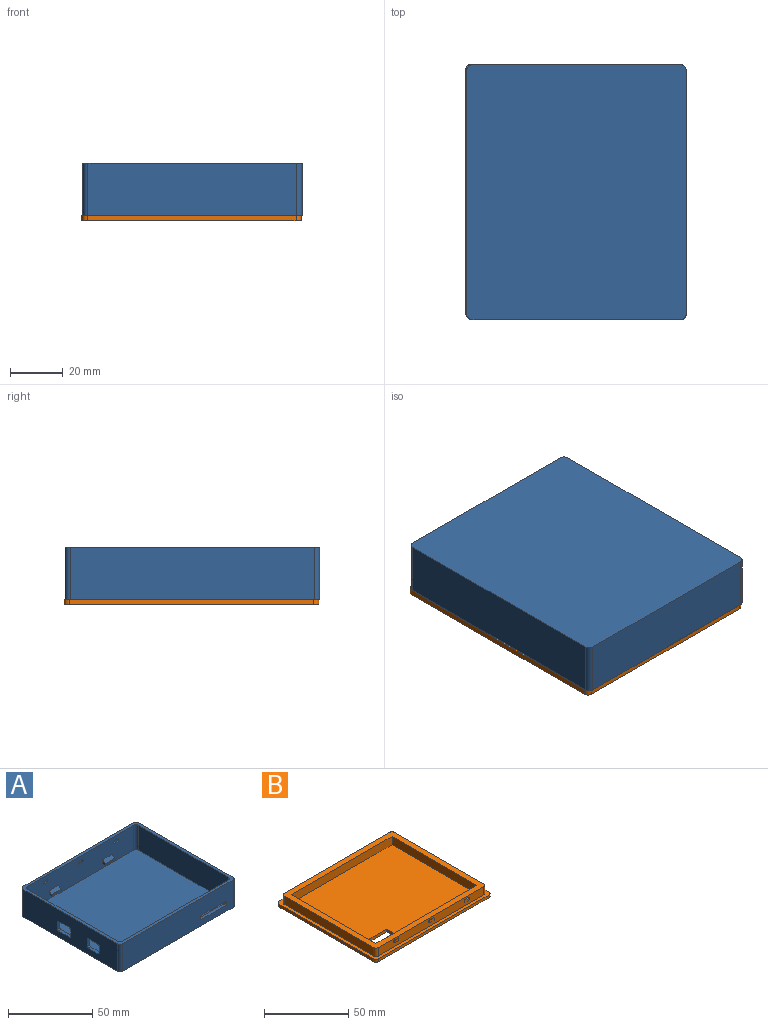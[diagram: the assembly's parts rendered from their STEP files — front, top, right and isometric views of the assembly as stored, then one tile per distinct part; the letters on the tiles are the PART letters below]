
ASSEMBLY  parts=2 mates=1
PART A: 89 faces, bbox 97x83.5x20 mm
  f0: plane 89x18mm, normal (0,1,0), area 1392.9mm2, adj f9,f10,f13,f14,f27,f28,f29,f30
  f1: plane 89x18mm, normal (0,-1,0), area 1530mm2, adj f9,f10,f11,f12,f43,f44,f45,f46
  f2: plane 93x20mm, normal (0,-1,0), area 1794.9mm2, adj f5,f9,f16,f17,f27,f28,f29,f30
  f3: plane 75.5x18mm, normal (1,0,0), area 1213.7mm2, adj f9,f10,f11,f14,f19,f20,f21,f22
  f4: plane 79.5x20mm, normal (-1,0,0), area 1444.7mm2, adj f5,f9,f15,f16,f19,f20,f21,f22
  f5: plane 97x83.5mm, normal (0,0,-1), area 8096.1mm2, adj f2,f4,f7,f8,f15,f16,f17,f18
  f6: plane 75.5x18mm, normal (-1,0,0), area 1359mm2, adj f9,f10,f12,f13
  f7: plane 93x20mm, normal (0,1,0), area 1860mm2, adj f5,f9,f15,f18
  f8: plane 79.5x20mm, normal (1,0,0), area 1590mm2, adj f5,f9,f17,f18
  f9: plane 97x83.5mm, normal (0,0,1), area 706mm2, adj f0,f1,f2,f3,f4,f6,f7,f8
  f10: plane 93x79.5mm, normal (0,0,1), area 7390.1mm2, adj f0,f1,f3,f6,f11,f12,f13,f14
  f11: cylinder r=2mm len=18mm, axis (0,0,-1), area 56.5mm2, adj f1,f3,f9,f10
  f12: cylinder r=2mm len=18mm, axis (0,0,1), area 56.5mm2, adj f1,f6,f9,f10
  f13: cylinder r=2mm len=18mm, axis (0,0,-1), area 56.5mm2, adj f0,f6,f9,f10
  f14: cylinder r=2mm len=18mm, axis (0,0,1), area 56.5mm2, adj f0,f3,f9,f10
  f15: cylinder r=2mm len=20mm, axis (0,0,1), area 62.8mm2, adj f4,f5,f7,f9
  f16: cylinder r=2mm len=20mm, axis (0,0,-1), area 62.8mm2, adj f2,f4,f5,f9
  f17: cylinder r=2mm len=20mm, axis (0,0,1), area 62.8mm2, adj f2,f5,f8,f9
  f18: cylinder r=2mm len=20mm, axis (0,0,-1), area 62.8mm2, adj f5,f7,f8,f9
  f19: plane 5x2mm, normal (0,1,0), area 10mm2, adj f3,f4,f35,f38
  f20: plane 9x2mm, normal (0,0,-1), area 18mm2, adj f3,f4,f35,f36
  f21: plane 5x2mm, normal (0,-1,0), area 10mm2, adj f3,f4,f36,f37
  f22: plane 9x2mm, normal (0,0,1), area 18mm2, adj f3,f4,f37,f38
  f23: plane 5x2mm, normal (0,1,0), area 10mm2, adj f3,f4,f39,f42
  f24: plane 8x2mm, normal (0,0,-1), area 16mm2, adj f3,f4,f41,f42
  f25: plane 5x2mm, normal (0,-1,0), area 10mm2, adj f3,f4,f40,f41
  f26: plane 8x2mm, normal (0,0,1), area 16mm2, adj f3,f4,f39,f40
  f27: plane 2x1mm, normal (-1,0,0), area 2mm2, adj f0,f2,f31,f34
  f28: plane 20x2mm, normal (0,0,-1), area 40mm2, adj f0,f2,f31,f32
  f29: plane 2x1mm, normal (1,0,0), area 2mm2, adj f0,f2,f32,f33
  f30: plane 20x2mm, normal (0,0,1), area 40mm2, adj f0,f2,f33,f34
  f31: cylinder r=1mm len=2mm, axis (0,-1,0), area 3.1mm2, adj f0,f2,f27,f28
  f32: cylinder r=1mm len=2mm, axis (0,1,0), area 3.1mm2, adj f0,f2,f28,f29
  f33: cylinder r=1mm len=2mm, axis (0,-1,0), area 3.1mm2, adj f0,f2,f29,f30
  f34: cylinder r=1mm len=2mm, axis (0,1,0), area 3.1mm2, adj f0,f2,f27,f30
  f35: cylinder r=1mm len=2mm, axis (-1,0,0), area 3.1mm2, adj f3,f4,f19,f20
  f36: cylinder r=1mm len=2mm, axis (1,0,0), area 3.1mm2, adj f3,f4,f20,f21
  f37: cylinder r=1mm len=2mm, axis (-1,0,0), area 3.1mm2, adj f3,f4,f21,f22
  f38: cylinder r=1mm len=2mm, axis (1,0,0), area 3.1mm2, adj f3,f4,f19,f22
  f39: cylinder r=1mm len=2mm, axis (1,0,0), area 3.1mm2, adj f3,f4,f23,f26
  f40: cylinder r=1mm len=2mm, axis (-1,0,0), area 3.1mm2, adj f3,f4,f25,f26
  f41: cylinder r=1mm len=2mm, axis (1,0,0), area 3.1mm2, adj f3,f4,f24,f25
  f42: cylinder r=1mm len=2mm, axis (-1,0,0), area 3.1mm2, adj f3,f4,f23,f24
  f43: plane 2x0.6mm, normal (-1,0,0), area 1.2mm2, adj f1,f44,f46,f47
  f44: plane 4x0.6mm, normal (0,0,-1), area 2.4mm2, adj f1,f43,f45,f47
  f45: plane 2x0.6mm, normal (1,0,0), area 1.2mm2, adj f1,f44,f46,f47
  f46: plane 4x0.6mm, normal (0,0,1), area 2.4mm2, adj f1,f43,f45,f47
  f47: plane 4x2mm, normal (0,-1,0), area 8mm2, adj f43,f44,f45,f46
  f48: plane 2x0.6mm, normal (-1,0,0), area 1.2mm2, adj f1,f49,f51,f52
  f49: plane 4x0.6mm, normal (0,0,-1), area 2.4mm2, adj f1,f48,f50,f52
  f50: plane 2x0.6mm, normal (1,0,0), area 1.2mm2, adj f1,f49,f51,f52
  f51: plane 4x0.6mm, normal (0,0,1), area 2.4mm2, adj f1,f48,f50,f52
  f52: plane 4x2mm, normal (0,-1,0), area 8mm2, adj f48,f49,f50,f51
  f53: plane 2x0.6mm, normal (-1,0,0), area 1.2mm2, adj f1,f54,f56,f57
  f54: plane 4x0.6mm, normal (0,0,-1), area 2.4mm2, adj f1,f53,f55,f57
  f55: plane 2x0.6mm, normal (1,0,0), area 1.2mm2, adj f1,f54,f56,f57
  f56: plane 4x0.6mm, normal (0,0,1), area 2.4mm2, adj f1,f53,f55,f57
  f57: plane 4x2mm, normal (0,-1,0), area 8mm2, adj f53,f54,f55,f56
  f58: plane 2x0.6mm, normal (1,0,0), area 1.2mm2, adj f0,f59,f61,f62
  f59: plane 4x0.6mm, normal (0,0,-1), area 2.4mm2, adj f0,f58,f60,f62
  f60: plane 2x0.6mm, normal (-1,0,0), area 1.2mm2, adj f0,f59,f61,f62
  f61: plane 4x0.6mm, normal (0,0,1), area 2.4mm2, adj f0,f58,f60,f62
  f62: plane 4x2mm, normal (0,1,0), area 8mm2, adj f58,f59,f60,f61
  f63: plane 2x0.6mm, normal (1,0,0), area 1.2mm2, adj f0,f64,f66,f67
  f64: plane 4x0.6mm, normal (0,0,-1), area 2.4mm2, adj f0,f63,f65,f67
  f65: plane 2x0.6mm, normal (-1,0,0), area 1.2mm2, adj f0,f64,f66,f67
  f66: plane 4x0.6mm, normal (0,0,1), area 2.4mm2, adj f0,f63,f65,f67
  f67: plane 4x2mm, normal (0,1,0), area 8mm2, adj f63,f64,f65,f66
  f68: plane 2x0.6mm, normal (1,0,0), area 1.2mm2, adj f0,f69,f71,f72
  f69: plane 4x0.6mm, normal (0,0,-1), area 2.4mm2, adj f0,f68,f70,f72
  f70: plane 2x0.6mm, normal (-1,0,0), area 1.2mm2, adj f0,f69,f71,f72
  f71: plane 4x0.6mm, normal (0,0,1), area 2.4mm2, adj f0,f68,f70,f72
  f72: plane 4x2mm, normal (0,1,0), area 8mm2, adj f68,f69,f70,f71
  f73: plane 3x2mm, normal (-1,0,0), area 4mm2, adj f1,f74,f76,f82
  f74: plane 8x2mm, normal (0,0,-1), area 16mm2, adj f1,f73,f75,f76
  f75: plane 3x2mm, normal (1,0,0), area 4mm2, adj f1,f74,f76,f82
  f76: plane 8x1mm, normal (0,-1,0), area 8mm2, adj f73,f74,f75,f82
  f77: plane 3x2mm, normal (1,0,0), area 4mm2, adj f1,f79,f80,f81
  f78: plane 3x2mm, normal (-1,0,0), area 4mm2, adj f1,f79,f80,f81
  f79: plane 8x2mm, normal (0,0,-1), area 16mm2, adj f1,f77,f78,f80
  f80: plane 8x1mm, normal (0,-1,0), area 8mm2, adj f77,f78,f79,f81
  f81: plane 8x2mm, normal (0,-0.71,0.71), area 22.6mm2, adj f1,f77,f78,f80
  f82: plane 8x2mm, normal (0,-0.71,0.71), area 22.6mm2, adj f1,f73,f75,f76
  f83: plane 3x3mm, normal (-1,0,0), area 7mm2, adj f0,f84,f86,f87,f88
  f84: plane 40x1mm, normal (0,0,1), area 40mm2, adj f0,f83,f85,f88
  f85: plane 3x3mm, normal (1,0,0), area 7mm2, adj f0,f84,f86,f87,f88
  f86: plane 40x3mm, normal (0,0,-1), area 120mm2, adj f0,f83,f85,f87
  f87: plane 40x1mm, normal (0,1,0), area 40mm2, adj f83,f85,f86,f88
  f88: plane 40x2mm, normal (0,0.71,0.71), area 113.1mm2, adj f83,f84,f85,f87
PART B: 58 faces, bbox 97x83.5x8 mm
  f0: plane 88.6x6mm, normal (0,1,0), area 514.3mm2, adj f5,f19,f22,f23,f43,f44,f45,f46
  f1: plane 79.5x2mm, normal (-1,0,0), area 159mm2, adj f5,f6,f24,f27
  f2: plane 93x2mm, normal (0,-1,0), area 186mm2, adj f5,f6,f24,f25
  f3: plane 79.5x2mm, normal (1,0,0), area 159mm2, adj f5,f6,f25,f26
  f4: plane 93x2mm, normal (0,1,0), area 186mm2, adj f5,f6,f26,f27
  f5: plane 97x83.5mm, normal (0,0,1), area 774.8mm2, adj f0,f1,f2,f3,f4,f14,f15,f16
  f6: plane 97x83.5mm, normal (0,0,-1), area 8006.1mm2, adj f1,f2,f3,f4,f7,f8,f9,f10
  f7: plane 15x2mm, normal (0,-1,0), area 30mm2, adj f6,f8,f10,f11
  f8: plane 6x2mm, normal (-1,0,0), area 12mm2, adj f6,f7,f9,f11
  f9: plane 15x2mm, normal (0,1,0), area 30mm2, adj f6,f8,f10,f11
  f10: plane 6x2mm, normal (1,0,0), area 12mm2, adj f6,f7,f9,f11
  f11: plane 84.6x71.1mm, normal (0,0,1), area 5925.1mm2, adj f7,f8,f9,f10,f12,f13,f17,f18
  f12: plane 71.1x6mm, normal (1,0,0), area 426.6mm2, adj f11,f17,f18,f19
  f13: plane 71.1x6mm, normal (-1,0,0), area 426.6mm2, adj f11,f17,f18,f19
  f14: plane 75.1x6mm, normal (-1,0,0), area 450.6mm2, adj f5,f19,f20,f23
  f15: plane 88.6x6mm, normal (0,-1,0), area 514.3mm2, adj f5,f19,f20,f21,f28,f29,f30,f31
  f16: plane 75.1x6mm, normal (1,0,0), area 450.6mm2, adj f5,f19,f21,f22
  f17: plane 84.6x6mm, normal (0,-1,0), area 507.6mm2, adj f11,f12,f13,f19
  f18: plane 84.6x6mm, normal (0,1,0), area 507.6mm2, adj f11,f12,f13,f19
  f19: plane 92.6x79.1mm, normal (0,0,1), area 1306.2mm2, adj f0,f12,f13,f14,f15,f16,f17,f18
  f20: cylinder r=2mm len=6mm, axis (0,0,-1), area 18.8mm2, adj f5,f14,f15,f19
  f21: cylinder r=2mm len=6mm, axis (0,0,1), area 18.8mm2, adj f5,f15,f16,f19
  f22: cylinder r=2mm len=6mm, axis (0,0,-1), area 18.8mm2, adj f0,f5,f16,f19
  f23: cylinder r=2mm len=6mm, axis (0,0,1), area 18.8mm2, adj f0,f5,f14,f19
  f24: cylinder r=2mm len=2mm, axis (0,0,-1), area 6.3mm2, adj f1,f2,f5,f6
  f25: cylinder r=2mm len=2mm, axis (0,0,-1), area 6.3mm2, adj f2,f3,f5,f6
  f26: cylinder r=2mm len=2mm, axis (0,0,1), area 6.3mm2, adj f3,f4,f5,f6
  f27: cylinder r=2mm len=2mm, axis (0,0,1), area 6.3mm2, adj f1,f4,f5,f6
  f28: plane 3.6x0.7mm, normal (0,0,-1), area 2.5mm2, adj f15,f29,f31,f32
  f29: plane 1.6x0.7mm, normal (1,0,0), area 1.1mm2, adj f15,f28,f30,f32
  f30: plane 3.6x0.7mm, normal (0,0,1), area 2.5mm2, adj f15,f29,f31,f32
  f31: plane 1.6x0.7mm, normal (-1,0,0), area 1.1mm2, adj f15,f28,f30,f32
  f32: plane 3.6x1.6mm, normal (0,-1,0), area 5.8mm2, adj f28,f29,f30,f31
  f33: plane 1.6x0.7mm, normal (1,0,0), area 1.1mm2, adj f15,f34,f36,f37
  f34: plane 3.6x0.7mm, normal (0,0,1), area 2.5mm2, adj f15,f33,f35,f37
  f35: plane 1.6x0.7mm, normal (-1,0,0), area 1.1mm2, adj f15,f34,f36,f37
  f36: plane 3.6x0.7mm, normal (0,0,-1), area 2.5mm2, adj f15,f33,f35,f37
  f37: plane 3.6x1.6mm, normal (0,-1,0), area 5.8mm2, adj f33,f34,f35,f36
  f38: plane 1.6x0.7mm, normal (1,0,0), area 1.1mm2, adj f15,f39,f41,f42
  f39: plane 3.6x0.7mm, normal (0,0,1), area 2.5mm2, adj f15,f38,f40,f42
  f40: plane 1.6x0.7mm, normal (-1,0,0), area 1.1mm2, adj f15,f39,f41,f42
  f41: plane 3.6x0.7mm, normal (0,0,-1), area 2.5mm2, adj f15,f38,f40,f42
  f42: plane 3.6x1.6mm, normal (0,-1,0), area 5.8mm2, adj f38,f39,f40,f41
  f43: plane 1.6x0.7mm, normal (-1,0,0), area 1.1mm2, adj f0,f44,f46,f47
  f44: plane 3.6x0.7mm, normal (0,0,1), area 2.5mm2, adj f0,f43,f45,f47
  f45: plane 1.6x0.7mm, normal (1,0,0), area 1.1mm2, adj f0,f44,f46,f47
  f46: plane 3.6x0.7mm, normal (0,0,-1), area 2.5mm2, adj f0,f43,f45,f47
  f47: plane 3.6x1.6mm, normal (0,1,0), area 5.8mm2, adj f43,f44,f45,f46
  f48: plane 1.6x0.7mm, normal (-1,0,0), area 1.1mm2, adj f0,f49,f51,f52
  f49: plane 3.6x0.7mm, normal (0,0,1), area 2.5mm2, adj f0,f48,f50,f52
  f50: plane 1.6x0.7mm, normal (1,0,0), area 1.1mm2, adj f0,f49,f51,f52
  f51: plane 3.6x0.7mm, normal (0,0,-1), area 2.5mm2, adj f0,f48,f50,f52
  f52: plane 3.6x1.6mm, normal (0,1,0), area 5.8mm2, adj f48,f49,f50,f51
  f53: plane 1.6x0.7mm, normal (-1,0,0), area 1.1mm2, adj f0,f54,f56,f57
  f54: plane 3.6x0.7mm, normal (0,0,1), area 2.5mm2, adj f0,f53,f55,f57
  f55: plane 1.6x0.7mm, normal (1,0,0), area 1.1mm2, adj f0,f54,f56,f57
  f56: plane 3.6x0.7mm, normal (0,0,-1), area 2.5mm2, adj f0,f53,f55,f57
  f57: plane 3.6x1.6mm, normal (0,1,0), area 5.8mm2, adj f53,f54,f55,f56
PLACE A rot(axis=(0.71,-0.71,0),180deg) t=(20.49,-33.9,-34.62)mm fixed
PLACE B rot(axis=(0,0,-1),90deg) t=(12.01,110.33,-56.62)mm
MATE slider A.f10 <-> B.f6  axis (0,0,-1) through (20.49,-33.9,-36.62)mm
